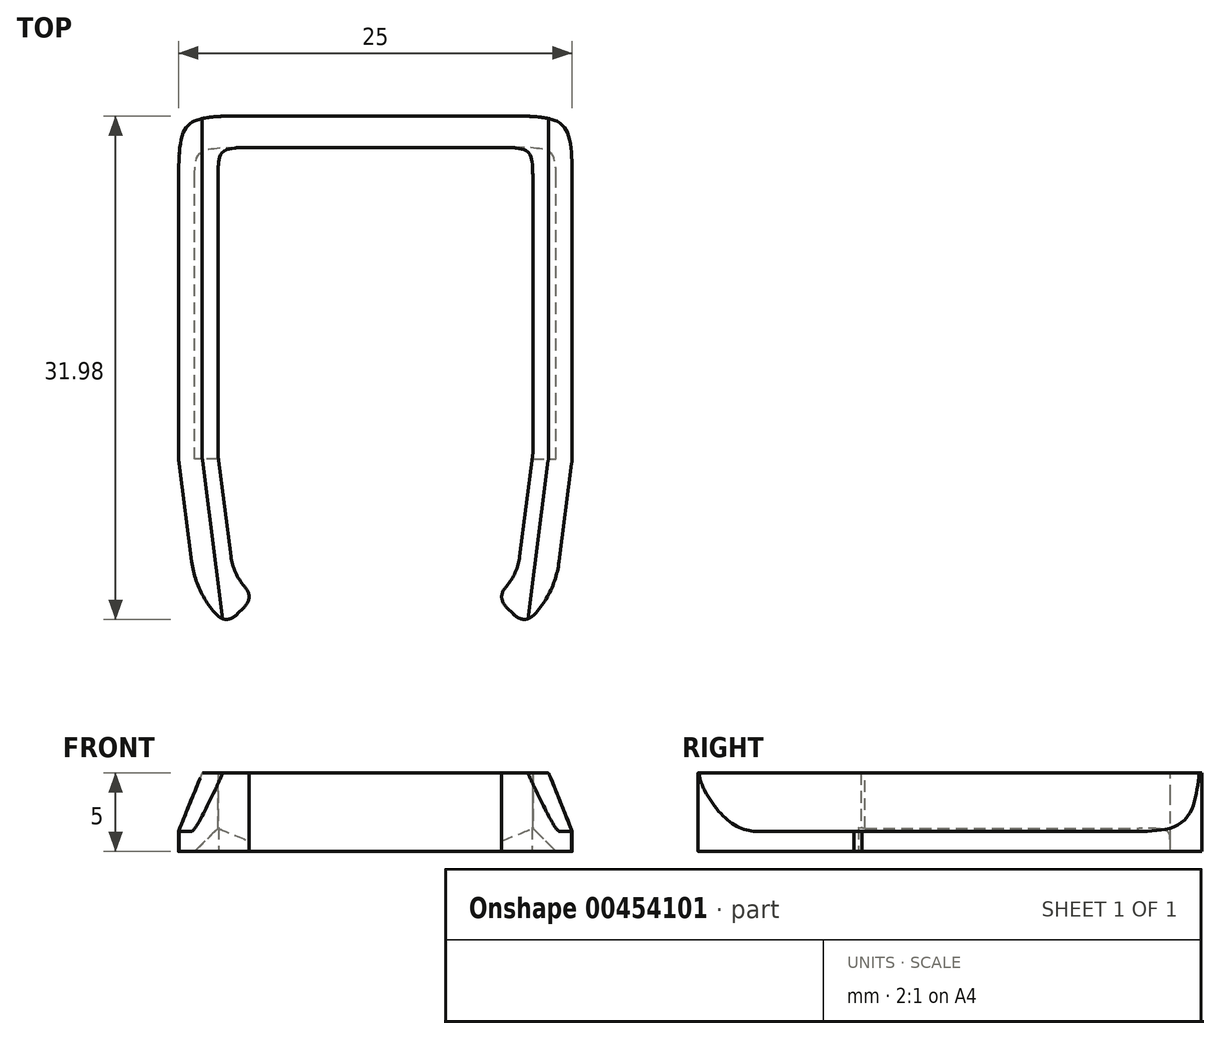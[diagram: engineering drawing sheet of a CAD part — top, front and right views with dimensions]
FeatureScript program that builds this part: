
annotation { "Feature Type Name" : "Feature", "Feature Type Description" : "" }
export const myFeature = defineFeature(function(context is Context, id is Id, definition is map)
    precondition{}
    {
        {
            var Q0;
            Q0=qCreatedBy(makeId("Top.planeOp"),FACE);
            var sketch = newSketch(context, id + "F0", { "sketchPlane" : qUnion([Q0])});
            skLineSegment(sketch, "E0", {"start": v(0, 0) * mm, "end": v(7.15, 0) * mm});
            skLineSegment(sketch, "E1", {"start": v(7.15, 0) * mm, "end": v(7.15, -3) * mm});
            skArc(sketch, "E2", {"start": v(8.15, -9.67) * mm, "mid": v(9.96, -5.99) * mm, "end": v(7.15, -3) * mm});
            skLineSegment(sketch, "E3", {"start": v(7.15, -3) * mm, "end": v(0, -3) * mm, "construction": true});
            skLineSegment(sketch, "E4", {"start": v(10, -6.52) * mm, "end": v(10, 0) * mm, "construction": true});
            skLineSegment(sketch, "E5", {"start": v(10, 0) * mm, "end": v(7.15, 0) * mm, "construction": true});
            skSolve(sketch);
        }
        {
            var Q0;
            Q0=qCreatedBy(makeId("Top.planeOp"),FACE);
            var sketch = newSketch(context, id + "F1", { "sketchPlane" : qUnion([Q0])});
            skLineSegment(sketch, "E6", {"start": v(0, 19) * mm, "end": v(0, 21) * mm});
            skLineSegment(sketch, "E7", {"start": v(0, 21) * mm, "end": v(12.5, 21) * mm});
            skLineSegment(sketch, "E8", {"start": v(9.42, -11.3) * mm, "end": v(7.62, -9.5) * mm});
            skLineSegment(sketch, "E9", {"start": v(0, 19) * mm, "end": v(10, 19) * mm});
            skLineSegment(sketch, "E10", {"start": v(10, -0.5) * mm, "end": v(9.17, -6.98) * mm});
            skArc(sketch, "E11", {"start": v(7.62, -9.5) * mm, "mid": v(8.67, -8.4) * mm, "end": v(9.17, -6.98) * mm});
            skLineSegment(sketch, "E12", {"start": v(12.5, -0.82) * mm, "end": v(11.67, -7.3) * mm});
            skArc(sketch, "E13", {"start": v(9.42, -11.3) * mm, "mid": v(10.94, -9.52) * mm, "end": v(11.67, -7.3) * mm});
            skLineSegment(sketch, "E14", {"start": v(12.5, 21) * mm, "end": v(12.5, -0.82) * mm});
            skLineSegment(sketch, "E15", {"start": v(10, 19) * mm, "end": v(10, -0.5) * mm});
            skLineSegment(sketch, "E16", {"start": v(10, 19) * mm, "end": v(12.5, 19) * mm, "construction": true});
            skLineSegment(sketch, "E17", {"start": v(10, -0.5) * mm, "end": v(12.5, -0.82) * mm, "construction": true});
            skSolve(sketch);
        }
        {
            var Q0;
            Q0=qSketchRegion(id+"F1",true);
            extrude(context, id + "F2", {"entities" : qUnion([Q0]), "depth" : 5 * mm});
        }
        {
            var Q0;
            Q0=makeQuery(id+"F2.opExtrude","SWEPT_EDGE",EDGE,{"disambiguationData":[OSD([sQuery(id+"F1.wireOp",EDGE,"E9"),sQuery(id+"F1.wireOp",EDGE,"E15")])]});
            var Q1;
            Q1=makeQuery(id+"F2.opExtrude","SWEPT_EDGE",EDGE,{"disambiguationData":[OSD([sQuery(id+"F1.wireOp",EDGE,"E10"),sQuery(id+"F1.wireOp",EDGE,"E15")])]});
            fillet(context, id + "F3", {"entities" : qUnion([Q0, Q1]), "radius" : 2 * mm, "tangentPropagation" : true, "rho" : .7, "crossSection" : FilletCrossSection.CONIC, "allowEdgeOverflow" : false});
        }
        {
            var Q0;
            Q0=makeQuery(id+"F2.opExtrude","SWEPT_EDGE",EDGE,{"disambiguationData":[OSD([sQuery(id+"F1.wireOp",EDGE,"E7"),sQuery(id+"F1.wireOp",EDGE,"E14")])]});
            var Q1;
            Q1=makeQuery(id+"F2.opExtrude","SWEPT_EDGE",EDGE,{"disambiguationData":[OSD([sQuery(id+"F1.wireOp",EDGE,"E12"),sQuery(id+"F1.wireOp",EDGE,"E14")])]});
            fillet(context, id + "F4", {"entities" : qUnion([Q0, Q1]), "radius" : 4 * mm, "tangentPropagation" : true, "rho" : .7, "crossSection" : FilletCrossSection.CONIC, "allowEdgeOverflow" : false});
        }
        {
            var Q0;
            Q0=makeQuery(id+"F2.opExtrude","SWEPT_FACE",FACE,{"disambiguationData":[OSD([sQuery(id+"F1.wireOp",EDGE,"E9")])]});
            var sketch = newSketch(context, id + "F5", { "sketchPlane" : qUnion([Q0])});
            skLineSegment(sketch, "E18.bottom", {"start": v(0, 2.5) * mm, "end": v(3, 2.5) * mm});
            skLineSegment(sketch, "E18.top", {"start": v(0, 0) * mm, "end": v(3, 0) * mm});
            skLineSegment(sketch, "E18.left", {"start": v(0, 2.5) * mm, "end": v(0, 0) * mm});
            skLineSegment(sketch, "E18.right", {"start": v(3, 2.5) * mm, "end": v(3, 0) * mm});
            skSolve(sketch);
        }
        {
            var Q0;
            Q0=makeQuery(id+"F13.opPattern","COPY",EDGE,{"derivedFrom":makeQuery(id+"F2.opExtrude","CAP_EDGE",EDGE,{"disambiguationData":[OSD([sQuery(id+"F1.wireOp",EDGE,"E12")])],"isStart":true}),"instanceName":"1"});
            var Q1;
            Q1=makeQuery(id+"F2.opExtrude","CAP_EDGE",EDGE,{"disambiguationData":[OSD([sQuery(id+"F1.wireOp",EDGE,"E12")])],"isStart":false});
            var Q2;
            Q2=makeQuery(id+"F2.opExtrude","CAP_EDGE",EDGE,{"disambiguationData":[OSD([sQuery(id+"F1.wireOp",EDGE,"E14")])],"isStart":false});
            chamfer(context, id + "F6", {"entities" : qUnion([Q0, Q1, Q2]), "chamferType" : ChamferType.OFFSET_ANGLE, "width" : 1.5 * mm, "oppositeDirection" : true, "angle" : 68 * degree});
        }
        {
            var Q0;
            {var subQ3=sQuery(id+"F5.wireOp",EDGE,"E18.bottom");Q0=makeQuery(id+"F5.imprint","IMPRINT",FACE,{"disambiguationData":[TD([[makeQuery(id+"F5.imprint","IMPRINT",EDGE,{"derivedFrom":subQ3}),1.0]])]});}
            var sketch = newSketch(context, id + "F7", { "sketchPlane" : qUnion([Q0])});
            skLineSegment(sketch, "E19", {"start": v(8, 3.48) * mm, "end": v(8, 0) * mm});
            skLineSegment(sketch, "E20", {"start": v(8, 0) * mm, "end": v(11.48, 0) * mm});
            skLineSegment(sketch, "E21", {"start": v(11.48, 0) * mm, "end": v(8, 3.48) * mm});
            skPoint(sketch, "E22", {"position": v(9.98, 0) * mm});
            skSolve(sketch);
        }
        {
            var Q0;
            Q0 = qSketchRegion(id + "F7", true);
            extrude(context, id + "F8", {"entities" : qUnion([Q0]), "operationType" : NewBodyOperationType.REMOVE, "depth" : 19.8 * mm});
        }
        {
            var Q0;
            Q0=qCreatedBy(makeId("Front.planeOp"),FACE);
            cPlane(context, id + "F9", {"entities" : qUnion([Q0]), "cplaneType" : CPlaneType.OFFSET, "offset" : 0 * mm, "oppositeDirection" : true, "width" : 150 * mm, "height" : 150 * mm});
        }
        {
            var Q0;
            Q0=qCreatedBy(id+"F9.planeOp",FACE);
            var sketch = newSketch(context, id + "F10", { "sketchPlane" : qUnion([Q0])});
            skLineSegment(sketch, "E23", {"start": v(16.37, 0) * mm, "end": v(14.33, 5) * mm});
            skLineSegment(sketch, "E24", {"start": v(14.33, 5) * mm, "end": v(11.1, 5) * mm});
            skLineSegment(sketch, "E25", {"start": v(16.37, 0) * mm, "end": v(12.6, 0) * mm});
            skLineSegment(sketch, "E26", {"start": v(12.6, 0) * mm, "end": v(11.1, 5) * mm});
            skLineSegment(sketch, "E27", {"start": v(12.6, 1.29) * mm, "end": v(11.1, 5) * mm, "construction": true});
            skSolve(sketch);
        }
        {
            var Q0;
            Q0=makeQuery(id+"F2.opExtrude","SWEPT_EDGE",EDGE,{"disambiguationData":[OSD([sQuery(id+"F1.wireOp",EDGE,"E8"),sQuery(id+"F1.wireOp",EDGE,"E11")])]});
            var Q1;
            Q1=makeQuery(id+"F2.opExtrude","SWEPT_EDGE",EDGE,{"disambiguationData":[OSD([sQuery(id+"F1.wireOp",EDGE,"E8"),sQuery(id+"F1.wireOp",EDGE,"E13")])]});
            var Q2;
            Q2=makeQuery(id+"FeDOwkYFawgQy55_1.opExtrude","CAP_EDGE",EDGE,{"disambiguationData":[OSD([sQuery(id+"F10.wireOp",EDGE,"E23")])],"isStart":true});
            var Q3;
            Q3=makeQuery(id+"FeDOwkYFawgQy55_1.opExtrude","CAP_EDGE",EDGE,{"disambiguationData":[OSD([sQuery(id+"F10.wireOp",EDGE,"E23")])],"isStart":false});
            var Q4;
            Q4=makeQuery(id+"FeDOwkYFawgQy55_1.boolean.opBoolean","INTERSECT",EDGE,{"derivedFrom":[makeQuery(id+"F6.opChamfer","BLEND_FACE",FACE,{"disambiguationData":[OSD([sQuery(id+"F1.wireOp",EDGE,"E12")])]}),makeQuery(id+"FeDOwkYFawgQy55_1.opExtrude","CAP_FACE",FACE,{"disambiguationData":[OSD([sQuery(id+"F10.wireOp",EDGE,"E23"),sQuery(id+"F10.wireOp",EDGE,"E24"),sQuery(id+"F10.wireOp",EDGE,"E25"),sQuery(id+"F10.wireOp",EDGE,"E26")])],"isStart":true})]});
            var Q5;
            Q5=makeQuery(id+"FeDOwkYFawgQy55_1.boolean.opBoolean","INTERSECT",EDGE,{"derivedFrom":[makeQuery(id+"F6.opChamfer","BLEND_FACE",FACE,{"disambiguationData":[OSD([sQuery(id+"F1.wireOp",EDGE,"E12")])]}),makeQuery(id+"FeDOwkYFawgQy55_1.opExtrude","CAP_FACE",FACE,{"disambiguationData":[OSD([sQuery(id+"F10.wireOp",EDGE,"E23"),sQuery(id+"F10.wireOp",EDGE,"E24"),sQuery(id+"F10.wireOp",EDGE,"E25"),sQuery(id+"F10.wireOp",EDGE,"E26")])],"isStart":false})]});
            var Q6;
            Q6=makeQuery(id+"FeDOwkYFawgQy55_1.boolean.opBoolean","INTERSECT",EDGE,{"derivedFrom":[makeQuery(id+"F2.opExtrude","SWEPT_FACE",FACE,{"disambiguationData":[OSD([sQuery(id+"F1.wireOp",EDGE,"E12")])]}),makeQuery(id+"FeDOwkYFawgQy55_1.opExtrude","CAP_FACE",FACE,{"disambiguationData":[OSD([sQuery(id+"F10.wireOp",EDGE,"E23"),sQuery(id+"F10.wireOp",EDGE,"E24"),sQuery(id+"F10.wireOp",EDGE,"E25"),sQuery(id+"F10.wireOp",EDGE,"E26")])],"isStart":false})]});
            var Q7;
            Q7=makeQuery(id+"FeDOwkYFawgQy55_1.boolean.opBoolean","INTERSECT",EDGE,{"derivedFrom":[makeQuery(id+"F2.opExtrude","SWEPT_FACE",FACE,{"disambiguationData":[OSD([sQuery(id+"F1.wireOp",EDGE,"E12")])]}),makeQuery(id+"FeDOwkYFawgQy55_1.opExtrude","CAP_FACE",FACE,{"disambiguationData":[OSD([sQuery(id+"F10.wireOp",EDGE,"E23"),sQuery(id+"F10.wireOp",EDGE,"E24"),sQuery(id+"F10.wireOp",EDGE,"E25"),sQuery(id+"F10.wireOp",EDGE,"E26")])],"isStart":true})]});
            fillet(context, id + "F11", {"entities" : qUnion([Q0, Q1, Q2, Q3, Q4, Q5, Q6, Q7]), "radius" : 1 * mm, "tangentPropagation" : true, "rho" : .5, "crossSection" : FilletCrossSection.CONIC, "allowEdgeOverflow" : false});
        }
        {
            var Q0;
            Q0=makeQuery(id+"F8.boolean.opBoolean","COPY",EDGE,{"derivedFrom":makeQuery(id+"F8.opExtrude","CAP_EDGE",EDGE,{"disambiguationData":[OSD([sQuery(id+"F7.wireOp",EDGE,"E21")])],"isStart":true})});
            fillet(context, id + "F12", {"entities" : qUnion([Q0]), "radius" : 2 * mm, "tangentPropagation" : true, "rho" : .7, "crossSection" : FilletCrossSection.CONIC, "allowEdgeOverflow" : false});
        }
        {
            var Q0;
            Q0=makeQuery(id+"F2.opExtrude","SWEPT_BODY",BODY,{"disambiguationData":[OSD([sQuery(id+"F1.wireOp",EDGE,"E6"),sQuery(id+"F1.wireOp",EDGE,"E7"),sQuery(id+"F1.wireOp",EDGE,"E8"),sQuery(id+"F1.wireOp",EDGE,"E9"),sQuery(id+"F1.wireOp",EDGE,"E10"),sQuery(id+"F1.wireOp",EDGE,"E11"),sQuery(id+"F1.wireOp",EDGE,"E12"),sQuery(id+"F1.wireOp",EDGE,"E13")])]});
            var Q1;
            Q1=makeQuery(id+"FEYfMAQslLhMSq6_1.boolean.opBoolean","MERGE",FACE,{"derivedFrom":[makeQuery(id+"F2.opExtrude","SWEPT_FACE",FACE,{"disambiguationData":[OSD([sQuery(id+"F1.wireOp",EDGE,"E6")])]}),makeQuery(id+"FEYfMAQslLhMSq6_1.opExtrude","SWEPT_FACE",FACE,{"disambiguationData":[OSD([sQuery(id+"F5.wireOp",EDGE,"E18.left")])]})]});
            mirror(context, id + "F13", {"operationType" : NewBodyOperationType.ADD, "entities" : qUnion([Q0]), "mirrorPlane" : qUnion([Q1])});
        }
    });
